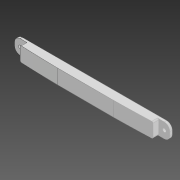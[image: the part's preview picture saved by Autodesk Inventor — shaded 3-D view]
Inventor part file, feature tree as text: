
AUTODESK INVENTOR PART (.ipt)
format: ipt  version: 2020 (Build 240168000, 168)  size: 143,872 bytes
history: native  units: mm
features: extrude x3, sketch x2, imported_body x1
ambient origin geometry x8: Origin, YZ Plane, XZ Plane, XY Plane, X Axis, Y Axis, Z Axis, Center Point
bodies: Solid1 (feature_tree)
feature tree (6):
  extrude  "BaseFeature"  Depth=3.0mm
  extrude  "Extrusion2"  Depth=10.0mm
  extrude  "Extrusion4"  Depth=10.0mm
  imported_body  "Base"
  sketch  "Sketch2"  dims[d0=128.0mm d1=3.0mm]
  sketch  "Sketch3"  dims[d2=3.0mm d3=5.0mm d4=5.0mm d5=5.0mm d6=5.0mm d7=5.0mm d8=6.5mm d9=6.5mm d10=2.0mm d11=0.0mm d12=1.0mm d13=1.0mm d14=6.0mm d15=0.0mm d17=1076.930462mm d22=1.0mm d23=1.0mm d24=10.0mm d25=0.0mm]
